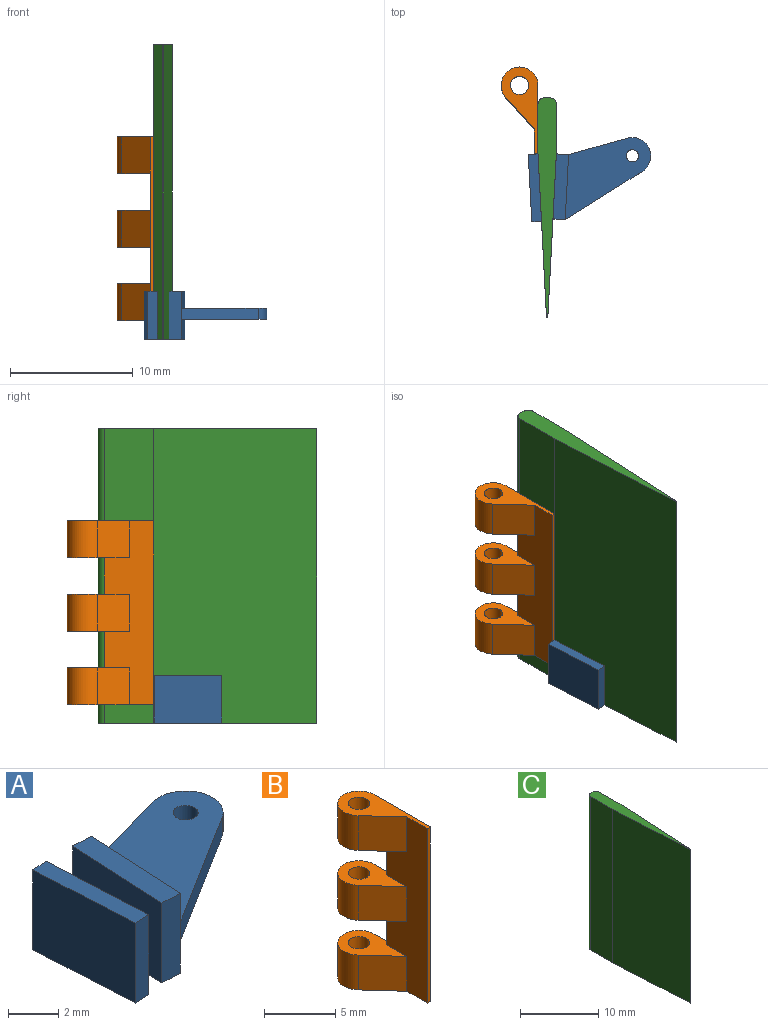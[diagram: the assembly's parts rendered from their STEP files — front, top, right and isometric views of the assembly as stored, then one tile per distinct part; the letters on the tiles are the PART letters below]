
ASSEMBLY  parts=3 mates=2
PART A: 23 faces, bbox 10x6.9x3.9 mm
  f0: plane 5.3x1.6mm, normal (1,-0.05,0), area 8.5mm2, adj f2,f4,f5,f11
  f1: plane 5.3x3.9mm, normal (-1,0.05,0), area 19.7mm2, adj f2,f4,f5,f6,f13,f14,f19,f20
  f2: plane 3.9x1mm, normal (0.05,1,0), area 3.9mm2, adj f0,f1,f3,f5,f6,f7
  f3: plane 5.3x1.4mm, normal (1,-0.05,0), area 7.4mm2, adj f2,f4,f6,f12
  f4: plane 3.9x1mm, normal (-0.05,-1,0), area 3.9mm2, adj f0,f1,f3,f5,f6,f9
  f5: plane 5.35x1.28mm, normal (0,0,-1), area 5.3mm2, adj f0,f1,f2,f4
  f6: plane 5.35x1.28mm, normal (0,0,1), area 5.3mm2, adj f1,f2,f3,f4
  f7: plane 4.8x1.34mm, normal (-0.27,0.96,0), area 4.5mm2, adj f2,f8,f11,f12
  f8: cylinder r=1.5mm len=2.77mm, axis (0,0,1), area 3.9mm2, adj f7,f9,f11,f12
  f9: plane 6.28x3.92mm, normal (0.53,-0.85,0), area 6.7mm2, adj f4,f8,f11,f12
  f10: cylinder r=0.5mm len=1mm, axis (0,0,1), area 2.8mm2, adj f11,f12
  f11: plane 6.98x6.7mm, normal (0,0,-1), area 25.5mm2, adj f0,f7,f8,f9,f10
  f12: plane 6.98x6.7mm, normal (0,0,1), area 25.5mm2, adj f3,f7,f8,f9,f10
  f13: plane 1.31x0.9mm, normal (-0.04,1,0), area 1.2mm2, adj f1,f15,f19,f20
  f14: plane 1.19x0.9mm, normal (0.04,-1,0), area 1.1mm2, adj f1,f15,f19,f20
  f15: plane 5.49x3.9mm, normal (1,0.05,0), area 20.4mm2, adj f13,f14,f16,f18,f19,f20,f21,f22
  f16: plane 3.9x0.79mm, normal (0.05,-1,0), area 3.1mm2, adj f15,f17,f21,f22
  f17: plane 5.49x3.9mm, normal (-1,-0.05,0), area 21.4mm2, adj f16,f18,f21,f22
  f18: plane 3.9x0.79mm, normal (-0.05,1,0), area 3.1mm2, adj f15,f17,f21,f22
  f19: plane 1.31x1.2mm, normal (0,0,-1), area 1.4mm2, adj f1,f13,f14,f15
  f20: plane 1.31x1.2mm, normal (0,0,1), area 1.4mm2, adj f1,f13,f14,f15
  f21: plane 5.53x1.08mm, normal (0,0,1), area 4.4mm2, adj f15,f16,f17,f18
  f22: plane 5.53x1.08mm, normal (0,0,-1), area 4.4mm2, adj f15,f16,f17,f18
PART B: 20 faces, bbox 3x7.1x15 mm
  f0: plane 3x0.3mm, normal (0,1,0), area 0.9mm2, adj f2,f3,f15,f19
  f1: plane 3x0.3mm, normal (0,1,0), area 0.9mm2, adj f2,f3,f10,f14
  f2: plane 15x5.57mm, normal (1,0,0), area 74.4mm2, adj f0,f1,f4,f5,f6,f8,f10,f12
  f3: plane 15x4.04mm, normal (-1,0,0), area 42.4mm2, adj f0,f1,f4,f5,f6,f7,f10,f11
  f4: plane 15x0.3mm, normal (0,-1,0), area 4.5mm2, adj f2,f3,f5,f6
  f5: plane 7.07x3mm, normal (0,0,-1), area 9mm2, adj f2,f3,f4,f7,f8,f9
  f6: plane 7.07x3mm, normal (0,0,1), area 9mm2, adj f2,f3,f4,f16,f17,f18
  f7: plane 3x2.55mm, normal (-0.74,-0.67,0), area 10.3mm2, adj f3,f5,f8,f10
  f8: cylinder r=1.5mm len=3mm, axis (0,0,1), area 17.5mm2, adj f2,f5,f7,f10
  f9: cylinder r=0.75mm len=3mm, axis (0,0,1), area 14.1mm2, adj f5,f10
  f10: plane 5.06x3mm, normal (0,0,1), area 7.8mm2, adj f1,f2,f3,f7,f8,f9
  f11: plane 3x2.55mm, normal (-0.74,-0.67,0), area 10.3mm2, adj f3,f12,f14,f15
  f12: cylinder r=1.5mm len=3mm, axis (0,0,1), area 17.5mm2, adj f2,f11,f14,f15
  f13: cylinder r=0.75mm len=3mm, axis (0,0,1), area 14.1mm2, adj f14,f15
  f14: plane 5.06x3mm, normal (0,0,-1), area 7.8mm2, adj f1,f2,f3,f11,f12,f13
  f15: plane 5.06x3mm, normal (0,0,1), area 7.8mm2, adj f0,f2,f3,f11,f12,f13
  f16: plane 3x2.55mm, normal (-0.74,-0.67,0), area 10.3mm2, adj f3,f6,f17,f19
  f17: cylinder r=1.5mm len=3mm, axis (0,0,1), area 17.5mm2, adj f2,f6,f16,f19
  f18: cylinder r=0.75mm len=3mm, axis (0,0,1), area 14.1mm2, adj f6,f19
  f19: plane 5.06x3mm, normal (0,0,-1), area 7.8mm2, adj f0,f2,f3,f16,f17,f18
PART C: 10 faces, bbox 1.5x17.8x24 mm
  f0: plane 24x0.5mm, normal (0,1,0), area 12mm2, adj f1,f4,f8,f9
  f1: plane 17.84x1.5mm, normal (0,0,-1), area 17.4mm2, adj f0,f2,f3,f5,f6,f7,f8,f9
  f2: plane 24x4.04mm, normal (1,0,0), area 96.9mm2, adj f1,f4,f6,f9
  f3: plane 24x0.11mm, normal (0,-1,0), area 2.5mm2, adj f1,f4,f6,f7
  f4: plane 17.84x1.5mm, normal (0,0,1), area 17.4mm2, adj f0,f2,f3,f5,f6,f7,f8,f9
  f5: plane 24x4.04mm, normal (-1,0,0), area 96.9mm2, adj f1,f4,f7,f8
  f6: plane 24x13.3mm, normal (1,-0.05,0), area 319.6mm2, adj f1,f2,f3,f4
  f7: plane 24x13.3mm, normal (-1,-0.05,0), area 319.6mm2, adj f1,f3,f4,f5
  f8: cylinder r=0.5mm len=24mm, axis (0,0,1), area 18.8mm2, adj f0,f1,f4,f5
  f9: cylinder r=0.5mm len=24mm, axis (0,0,-1), area 18.8mm2, adj f0,f1,f2,f4
PLACE A t=(2.63,3.43,-7.69)mm
PLACE B t=(2.63,3.43,-5.79)mm
PLACE C t=(2.63,3.43,-6.29)mm
MATE fastened C.f6 <-> A.f1  axis (1,-0.05,0) through (3.38,14.73,23.71)mm
MATE fastened C.f5 <-> B.f2  axis (-1,0,0) through (1.88,18.77,35.71)mm
